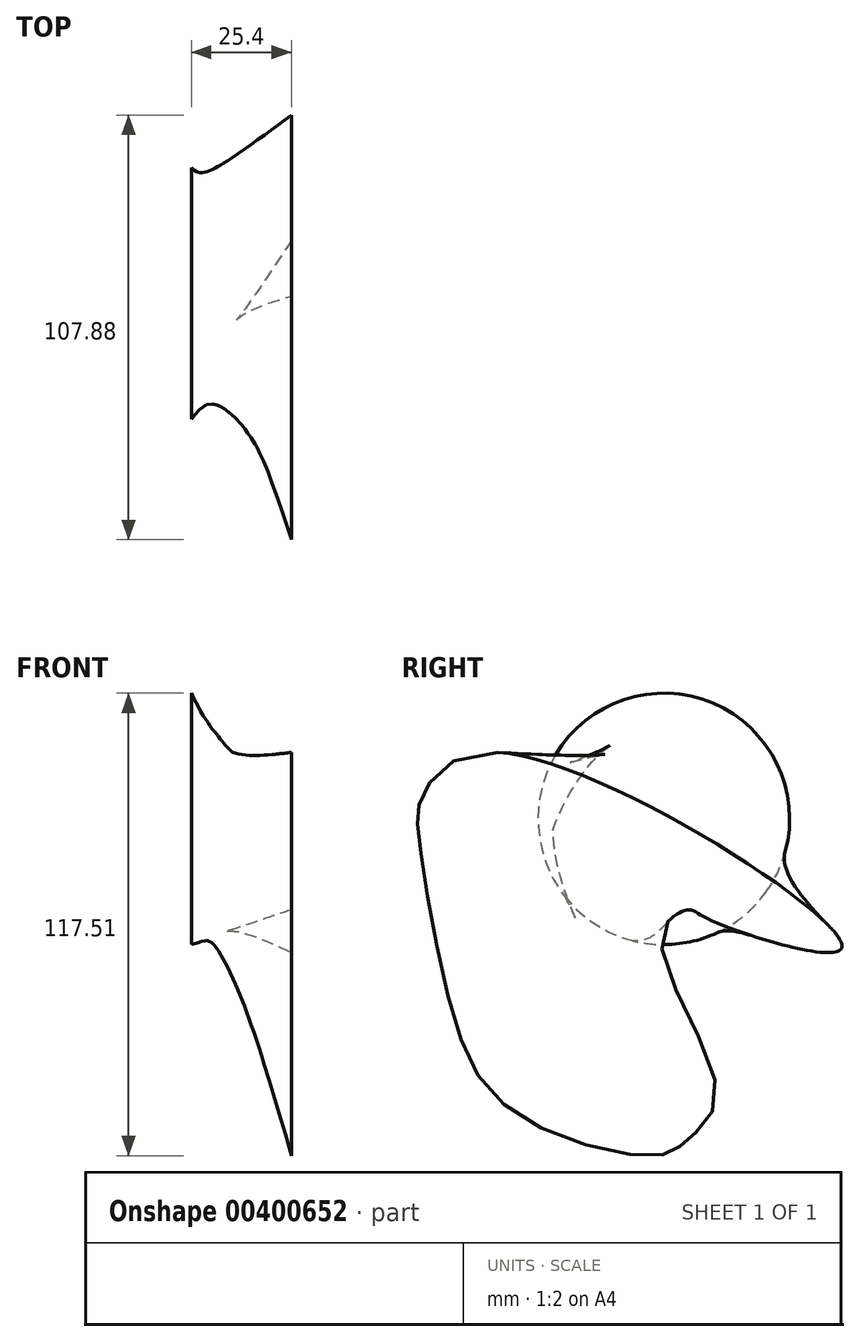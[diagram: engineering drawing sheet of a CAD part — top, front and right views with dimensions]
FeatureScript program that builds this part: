
annotation { "Feature Type Name" : "Feature", "Feature Type Description" : "" }
export const myFeature = defineFeature(function(context is Context, id is Id, definition is map)
    precondition{}
    {
        {
            var Q0;
            Q0=qCreatedBy(makeId("Right.planeOp"),FACE);
            cPlane(context, id + "F0", {"entities" : qUnion([Q0]), "cplaneType" : CPlaneType.OFFSET, "offset" : 25.4 * mm, "width" : 152.4 * mm, "height" : 152.4 * mm});
        }
        {
            var Q0;
            Q0=qCreatedBy(makeId("Right.planeOp"),FACE);
            var sketch = newSketch(context, id + "F1", { "sketchPlane" : qUnion([Q0])});
            skCircle(sketch, "E0", {"center": v(-6.1, 37.95) * mm, "radius": 31.94 * mm});
            skSolve(sketch);
        }
        {
            var Q0;
            Q0=qCreatedBy(id+"F0.planeOp",FACE);
            var sketch = newSketch(context, id + "F2", { "sketchPlane" : qUnion([Q0])});
            skFitSpline(sketch, "E1", {"points": [v(39.04, 5.09) * mm, v(-47.66, 54.78) * mm, v(-67.8, 43) * mm, v(-68.42, 34.14) * mm, v(-60.48, -8.96) * mm, v(-42.77, -37.55) * mm, v(-6.75, -47.45) * mm, v(0, -43.46) * mm, v(7.3, -31.2) * mm, v(-6.75, 7.89) * mm, v(0, 14.82) * mm, v(4.85, 12.66) * mm, v(39.04, 5.09) * mm]});
            skSolve(sketch);
        }
        {
            var Q0;
            Q0=makeQuery(id+"F2.imprint","IMPRINT",FACE,{"disambiguationData":[TD([[makeQuery(id+"F2.imprint","IMPRINT",EDGE,{"derivedFrom":sQuery(id+"F2.wireOp",EDGE,"E1")}),1.0]])]});
            var Q1;
            Q1=makeQuery(id+"F1.imprint","IMPRINT",FACE,{"disambiguationData":[TD([[makeQuery(id+"F1.imprint","IMPRINT",EDGE,{"derivedFrom":sQuery(id+"F1.wireOp",EDGE,"E0")}),1.0]])]});
            loft(context, id + "F3", {"sheetProfilesArray" : [{ "sheetProfileEntities" : qUnion([Q0]) }, { "sheetProfileEntities" : qUnion([Q1]) }]});
        }
    });
